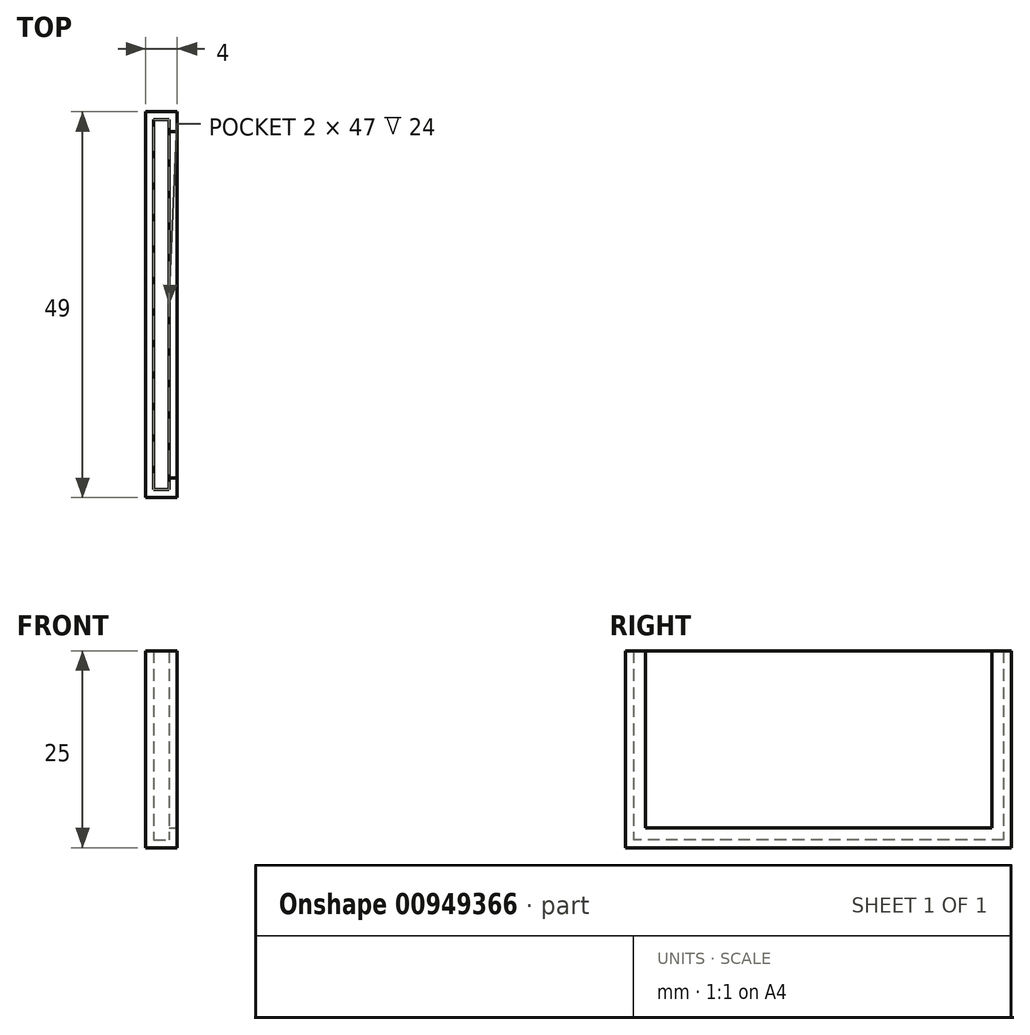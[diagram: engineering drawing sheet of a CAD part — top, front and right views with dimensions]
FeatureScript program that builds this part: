
annotation { "Feature Type Name" : "Feature", "Feature Type Description" : "" }
export const myFeature = defineFeature(function(context is Context, id is Id, definition is map)
    precondition{}
    {
        {
            var Q0;
            Q0=qCreatedBy(makeId("Top.planeOp"),FACE);
            var sketch = newSketch(context, id + "F0", { "sketchPlane" : qUnion([Q0])});
            skLineSegment(sketch, "E0.bottom", {"start": v(1, 23.5) * mm, "end": v(3, 23.5) * mm});
            skLineSegment(sketch, "E0.top", {"start": v(1, -23.5) * mm, "end": v(3, -23.5) * mm});
            skLineSegment(sketch, "E0.left", {"start": v(1, 23.5) * mm, "end": v(1, -23.5) * mm});
            skLineSegment(sketch, "E0.right", {"start": v(3, 23.5) * mm, "end": v(3, -23.5) * mm});
            skLineSegment(sketch, "E1.0", {"start": v(4, 24.5) * mm, "end": v(4, -24.5) * mm});
            skLineSegment(sketch, "E1.1", {"start": v(0, 24.5) * mm, "end": v(4, 24.5) * mm});
            skLineSegment(sketch, "E1.2", {"start": v(0, 24.5) * mm, "end": v(0, -24.5) * mm});
            skLineSegment(sketch, "E1.3", {"start": v(0, -24.5) * mm, "end": v(4, -24.5) * mm});
            skPoint(sketch, "E2", {"position": v(0, 0) * mm});
            skSolve(sketch);
        }
        {
            var Q0;
            {var subQ4=sQuery(id+"F0.wireOp",EDGE,"E0.bottom");Q0=makeQuery(id+"F0.imprint","IMPRINT",FACE,{"disambiguationData":[TD([[makeQuery(id+"F0.imprint","IMPRINT",EDGE,{"derivedFrom":subQ4}),1.0]])]});}
            var Q1;
            {var subQ0=sQuery(id+"F0.wireOp",EDGE,"E1.2");var subQ1=sQuery(id+"F0.wireOp",EDGE,"vD05sDmF-Ds0J-ag7c-iMKa-CvoiMpdynAw2.top");var subQ2=makeQuery(id+"F0.imprint","INTERSECT",VERTEX,{"derivedFrom":[subQ1,subQ0]});Q1=makeQuery(id+"F0.imprint","IMPRINT",FACE,{"disambiguationData":[TD([[makeQuery(id+"F0.imprint","IMPRINT",EDGE,{"disambiguationData":[TD([[subQ2,-1.0]])],"derivedFrom":subQ1}),1.0]])]});}
            var Q2;
            {var subQ0=sQuery(id+"F0.wireOp",EDGE,"E1.0");var subQ1=sQuery(id+"F0.wireOp",EDGE,"vD05sDmF-Ds0J-ag7c-iMKa-CvoiMpdynAw2.top");var subQ2=makeQuery(id+"F0.imprint","INTERSECT",VERTEX,{"derivedFrom":[subQ1,subQ0]});Q2=makeQuery(id+"F0.imprint","IMPRINT",FACE,{"disambiguationData":[TD([[makeQuery(id+"F0.imprint","IMPRINT",EDGE,{"disambiguationData":[TD([[subQ2,1.0]])],"derivedFrom":subQ1}),1.0]])]});}
            var Q3;
            {var subQ0=sQuery(id+"F0.wireOp",EDGE,"E1.2");var subQ1=sQuery(id+"F0.wireOp",EDGE,"vD05sDmF-Ds0J-ag7c-iMKa-CvoiMpdynAw2.top");var subQ2=makeQuery(id+"F0.imprint","INTERSECT",VERTEX,{"derivedFrom":[subQ1,subQ0]});Q3=makeQuery(id+"F0.imprint","IMPRINT",FACE,{"disambiguationData":[TD([[makeQuery(id+"F0.imprint","IMPRINT",EDGE,{"disambiguationData":[TD([[subQ2,-1.0]])],"derivedFrom":subQ1}),-1.0]])]});}
            var Q4;
            {var subQ0=sQuery(id+"F0.wireOp",EDGE,"E1.0");var subQ1=sQuery(id+"F0.wireOp",EDGE,"vD05sDmF-Ds0J-ag7c-iMKa-CvoiMpdynAw2.top");var subQ2=makeQuery(id+"F0.imprint","INTERSECT",VERTEX,{"derivedFrom":[subQ1,subQ0]});Q4=makeQuery(id+"F0.imprint","IMPRINT",FACE,{"disambiguationData":[TD([[makeQuery(id+"F0.imprint","IMPRINT",EDGE,{"disambiguationData":[TD([[subQ2,1.0]])],"derivedFrom":subQ1}),-1.0]])]});}
            var Q5;
            {var subQ5=sQuery(id+"F0.wireOp",EDGE,"E0.top");Q5=makeQuery(id+"F0.imprint","IMPRINT",FACE,{"disambiguationData":[TD([[makeQuery(id+"F0.imprint","IMPRINT",EDGE,{"derivedFrom":subQ5}),-1.0]])]});}
            extrude(context, id + "F1", {"entities" : qUnion([Q0, Q1, Q2, Q3, Q4, Q5]), "depth" : 25 * mm, "offsetDistance" : 25 * mm});
        }
        {
            var Q0;
            Q0=makeQuery(id+"F1.boolean.opBoolean","MERGE",FACE,{"derivedFrom":[makeQuery(id+"FbVtPxxAJ0qM1ay_1.opExtrude","SWEPT_FACE",FACE,{"disambiguationData":[OSD([sQuery(id+"Fe1X3ewoQiu8z6K_1.wireOp",EDGE,"E1HUhRQq-UAxI-3gm9-UwcN-w2k12ITGU1h4.right")])]}),makeQuery(id+"F1.opExtrude","SWEPT_FACE",FACE,{"disambiguationData":[OSD([sQuery(id+"F0.wireOp",EDGE,"E1.0")])]})]});
            var sketch = newSketch(context, id + "F2", { "sketchPlane" : qUnion([Q0])});
            skLineSegment(sketch, "E3.bottom", {"start": v(-22, 25) * mm, "end": v(22, 25) * mm});
            skLineSegment(sketch, "E3.top", {"start": v(-22, 2.5) * mm, "end": v(22, 2.5) * mm});
            skLineSegment(sketch, "E3.left", {"start": v(-22, 25) * mm, "end": v(-22, 2.5) * mm});
            skLineSegment(sketch, "E3.right", {"start": v(22, 25) * mm, "end": v(22, 2.5) * mm});
            skSolve(sketch);
        }
        {
            var Q0;
            Q0 = qSketchRegion(id + "F2", true);
            extrude(context, id + "F3", {"entities" : qUnion([Q0]), "operationType" : NewBodyOperationType.REMOVE, "oppositeDirection" : true, "depth" : 2 * mm, "offsetDistance" : 25 * mm});
        }
        {
            var Q0;
            {var subQ0=sQuery(id+"F0.wireOp",EDGE,"E0.top");Q0=makeQuery(id+"F0.imprint","IMPRINT",FACE,{"disambiguationData":[TD([[makeQuery(id+"F0.imprint","IMPRINT",EDGE,{"derivedFrom":subQ0}),1.0]])]});}
            var Q1;
            {var subQ0=sQuery(id+"F0.wireOp",EDGE,"E0.bottom");Q1=makeQuery(id+"F0.imprint","IMPRINT",FACE,{"disambiguationData":[TD([[makeQuery(id+"F0.imprint","IMPRINT",EDGE,{"derivedFrom":subQ0}),-1.0]])]});}
            var Q2;
            {var subQ0=sQuery(id+"F0.wireOp",EDGE,"E0.left");var subQ1=sQuery(id+"F0.wireOp",EDGE,"vD05sDmF-Ds0J-ag7c-iMKa-CvoiMpdynAw2.top");var subQ2=makeQuery(id+"F0.imprint","INTERSECT",VERTEX,{"derivedFrom":[subQ1,subQ0]});Q2=makeQuery(id+"F0.imprint","IMPRINT",FACE,{"disambiguationData":[TD([[makeQuery(id+"F0.imprint","IMPRINT",EDGE,{"disambiguationData":[TD([[subQ2,-1.0]])],"derivedFrom":subQ1}),1.0]])]});}
            var Q3;
            {var subQ0=sQuery(id+"F0.wireOp",EDGE,"E0.left");var subQ1=sQuery(id+"F0.wireOp",EDGE,"vD05sDmF-Ds0J-ag7c-iMKa-CvoiMpdynAw2.top");var subQ2=makeQuery(id+"F0.imprint","INTERSECT",VERTEX,{"derivedFrom":[subQ1,subQ0]});Q3=makeQuery(id+"F0.imprint","IMPRINT",FACE,{"disambiguationData":[TD([[makeQuery(id+"F0.imprint","IMPRINT",EDGE,{"disambiguationData":[TD([[subQ2,-1.0]])],"derivedFrom":subQ1}),-1.0]])]});}
            extrude(context, id + "F4", {"entities" : qUnion([Q0, Q1, Q2, Q3]), "operationType" : NewBodyOperationType.ADD, "depth" : 1 * mm, "offsetDistance" : 25 * mm});
        }
    });
